# Revit family: FantiniCosmi_BIM_A95A
name_source: partatom
category: Generic Models
units: mm (PartAtom-declared; Revit-internal decimal feet)

## family parameters
Always vertical = Yes
Can host rebar = No
Cut with Voids When Loaded = No
Part Type = Normal
Room Calculation Point = No
Round Connector Dimension = Use Diameter
Shared = No
Work Plane-Based = No

## types (1)
- Standard
    Cable length = 3 mt
    Cable type = PVC
    Catalog web link = https://www.fantinicosmi.it
    Conformity with = EN 60730-1, 60730-2-16
    Default Elevation = 0 mm  [stored 0 ft]
    Designer = Carniti
    Homologation = TÜV
    Max Pressure = 60
    Part Number = A95A
    Protection degree = IP68
    Weight = 0.7 Kg

note: source unit labels omitted for Max Pressure — the stored unit's dimension contradicts the parameter name (converter mislabeling)

note: [stored X ft] marks values corroborated as IEEE doubles in the binary element streams (Revit-internal decimal feet)

## geometry (parser evidence)
native form markers: Sweep x3
no freeform markers — native parametric forms only
